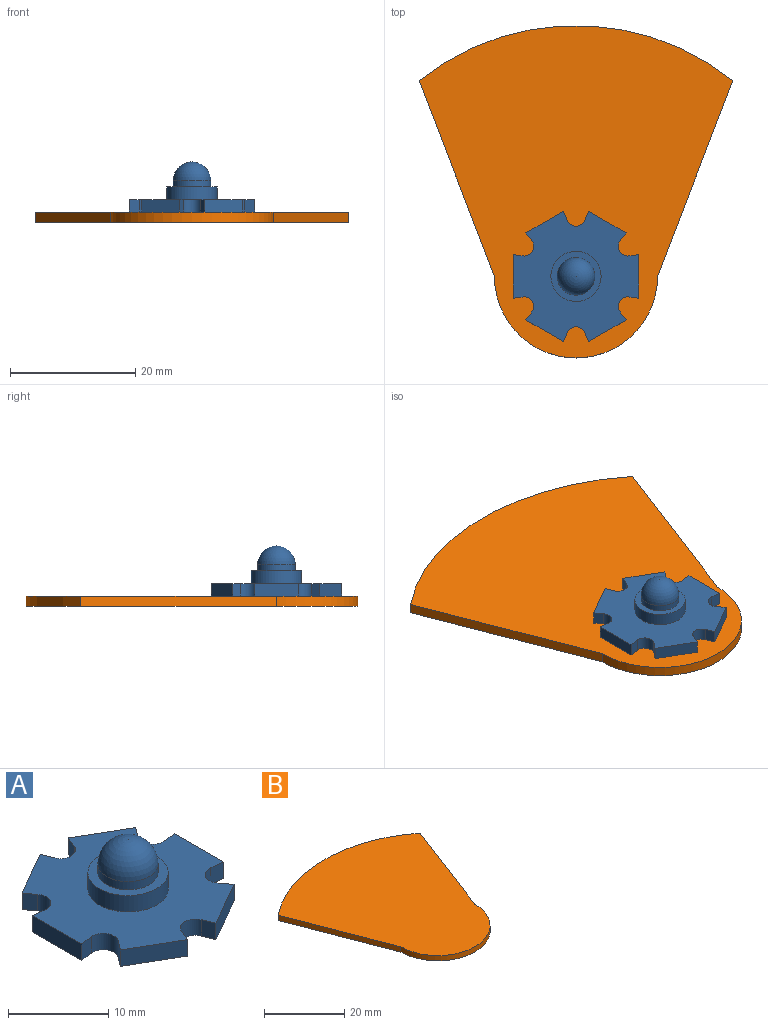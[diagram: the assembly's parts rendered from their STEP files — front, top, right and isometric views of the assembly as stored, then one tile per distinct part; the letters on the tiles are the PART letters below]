
ASSEMBLY  parts=2 mates=1
PART A: 30 faces, bbox 20x20.8x8 mm
  f0: cylinder r=1.5mm len=2.77mm, axis (0,0,-1), area 7mm2, adj f1,f23,f24,f25
  f1: plane 2x1.47mm, normal (-0.92,-0.39,0), area 3.2mm2, adj f0,f2,f24,f25
  f2: plane 6x3.46mm, normal (0.5,-0.87,0), area 13.9mm2, adj f1,f3,f24,f25
  f3: plane 2x1.27mm, normal (0.8,0.61,0), area 3.2mm2, adj f2,f4,f24,f25
  f4: cylinder r=1.5mm len=2.41mm, axis (0,0,-1), area 7mm2, adj f3,f5,f24,f25
  f5: plane 2x1.58mm, normal (-0.13,-0.99,0), area 3.2mm2, adj f4,f6,f24,f25
  f6: plane 6.93x2mm, normal (1,0,0), area 13.9mm2, adj f5,f7,f24,f25
  f7: plane 2x1.58mm, normal (-0.13,0.99,0), area 3.2mm2, adj f6,f8,f24,f25
  f8: cylinder r=1.5mm len=2.41mm, axis (0,0,-1), area 7mm2, adj f7,f9,f24,f25
  f9: plane 2x1.27mm, normal (0.8,-0.61,0), area 3.2mm2, adj f8,f10,f24,f25
  f10: plane 6x3.46mm, normal (0.5,0.87,0), area 13.9mm2, adj f9,f11,f24,f25
  f11: plane 2x1.47mm, normal (-0.92,0.39,0), area 3.2mm2, adj f10,f12,f24,f25
  f12: cylinder r=1.5mm len=2.77mm, axis (0,0,-1), area 7mm2, adj f11,f13,f24,f25
  f13: plane 2x1.47mm, normal (0.92,0.39,0), area 3.2mm2, adj f12,f14,f24,f25
  f14: plane 6x3.46mm, normal (-0.5,0.87,0), area 13.9mm2, adj f13,f15,f24,f25
  f15: plane 2x1.27mm, normal (-0.8,-0.61,0), area 3.2mm2, adj f14,f16,f24,f25
  f16: cylinder r=1.5mm len=2.41mm, axis (0,0,-1), area 7mm2, adj f15,f17,f24,f25
  f17: plane 2x1.58mm, normal (0.13,0.99,0), area 3.2mm2, adj f16,f18,f24,f25
  f18: plane 6.93x2mm, normal (-1,0,0), area 13.9mm2, adj f17,f19,f24,f25
  f19: plane 2x1.58mm, normal (0.13,-0.99,0), area 3.2mm2, adj f18,f20,f24,f25
  f20: cylinder r=1.5mm len=2.41mm, axis (0,0,-1), area 7mm2, adj f19,f21,f24,f25
  f21: plane 2x1.27mm, normal (-0.8,0.61,0), area 3.2mm2, adj f20,f22,f24,f25
  f22: plane 6x3.46mm, normal (-0.5,-0.87,0), area 13.9mm2, adj f21,f23,f24,f25
  f23: plane 2x1.47mm, normal (0.92,-0.39,0), area 3.2mm2, adj f0,f22,f24,f25
  f24: plane 20.78x20mm, normal (0,0,1), area 241.4mm2, adj f0,f1,f2,f3,f4,f5,f6,f7
  f25: plane 20.78x20mm, normal (0,0,-1), area 291.6mm2, adj f0,f1,f2,f3,f4,f5,f6,f7
  f26: cylinder r=4mm len=8mm, axis (0,0,-1), area 50.3mm2, adj f24,f27
  f27: plane 8x8mm, normal (0,0,1), area 22mm2, adj f26,f28
  f28: cylinder r=3mm len=6mm, axis (0,0,-1), area 18.8mm2, adj f27,f29
  f29: sphere r=3mm, area 56.5mm2, adj f28
PART B: 6 faces, bbox 50x53x1.6 mm
  f0: cylinder r=40mm len=50mm, axis (0,0,-1), area 86.4mm2, adj f1,f3,f4,f5
  f1: plane 31.23x12mm, normal (-0.93,-0.36,0), area 53.5mm2, adj f0,f2,f4,f5
  f2: cylinder r=13mm len=26mm, axis (0,0,-1), area 65.3mm2, adj f1,f3,f4,f5
  f3: plane 31.23x12mm, normal (0.93,-0.36,0), area 53.5mm2, adj f0,f2,f4,f5
  f4: plane 53x50mm, normal (0,0,1), area 1751.6mm2, adj f0,f1,f2,f3
  f5: plane 53x50mm, normal (0,0,-1), area 1751.6mm2, adj f0,f1,f2,f3
PLACE A t=(6.95,-6.37,7.72)mm
PLACE B t=(6.95,-6.37,6.12)mm fixed
MATE fastened B.f2 <-> A.f28  axis (0,0,1) through (6.95,-6.37,7.72)mm
